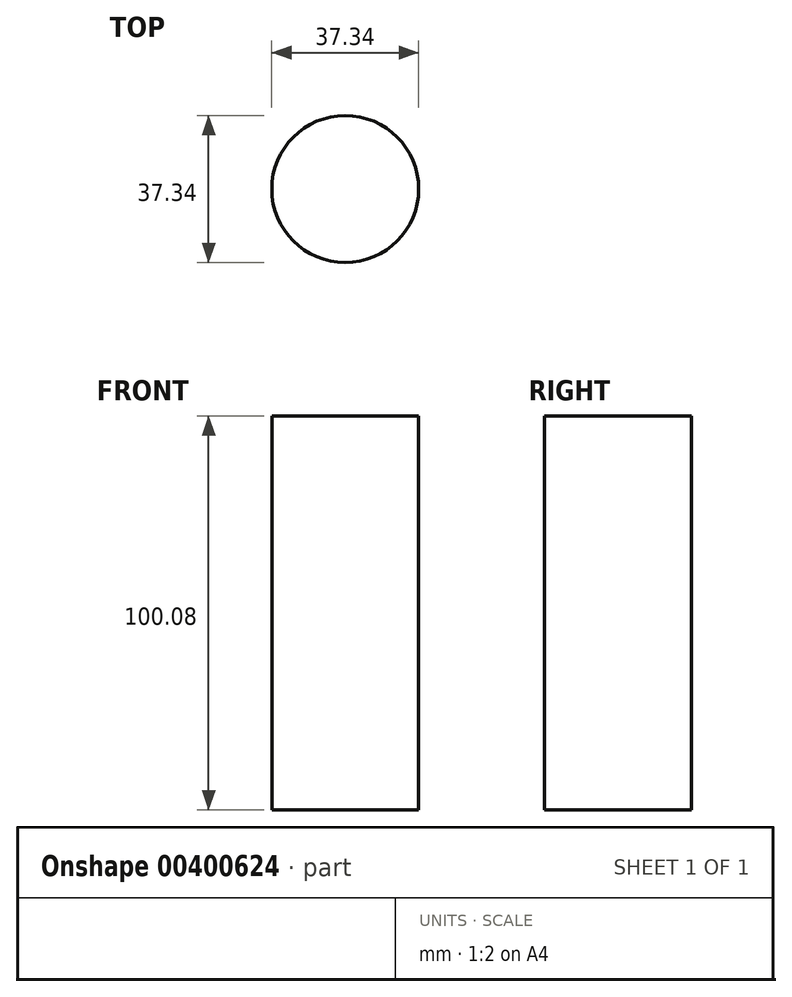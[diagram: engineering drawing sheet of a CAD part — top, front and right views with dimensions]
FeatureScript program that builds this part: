
annotation { "Feature Type Name" : "Feature", "Feature Type Description" : "" }
export const myFeature = defineFeature(function(context is Context, id is Id, definition is map)
    precondition{}
    {
        {
            var Q0;
            Q0=qCreatedBy(makeId("Top.planeOp"),FACE);
            var sketch = newSketch(context, id + "F0", { "sketchPlane" : qUnion([Q0])});
            skCircle(sketch, "E0", {"center": v(0, 0) * mm, "radius": 18.67 * mm});
            skSolve(sketch);
        }
        {
            var Q0;
            Q0 = qSketchRegion(id + "F0", true);
            extrude(context, id + "F1", {"entities" : qUnion([Q0]), "depth" : 100.08 * mm});
        }
    });
